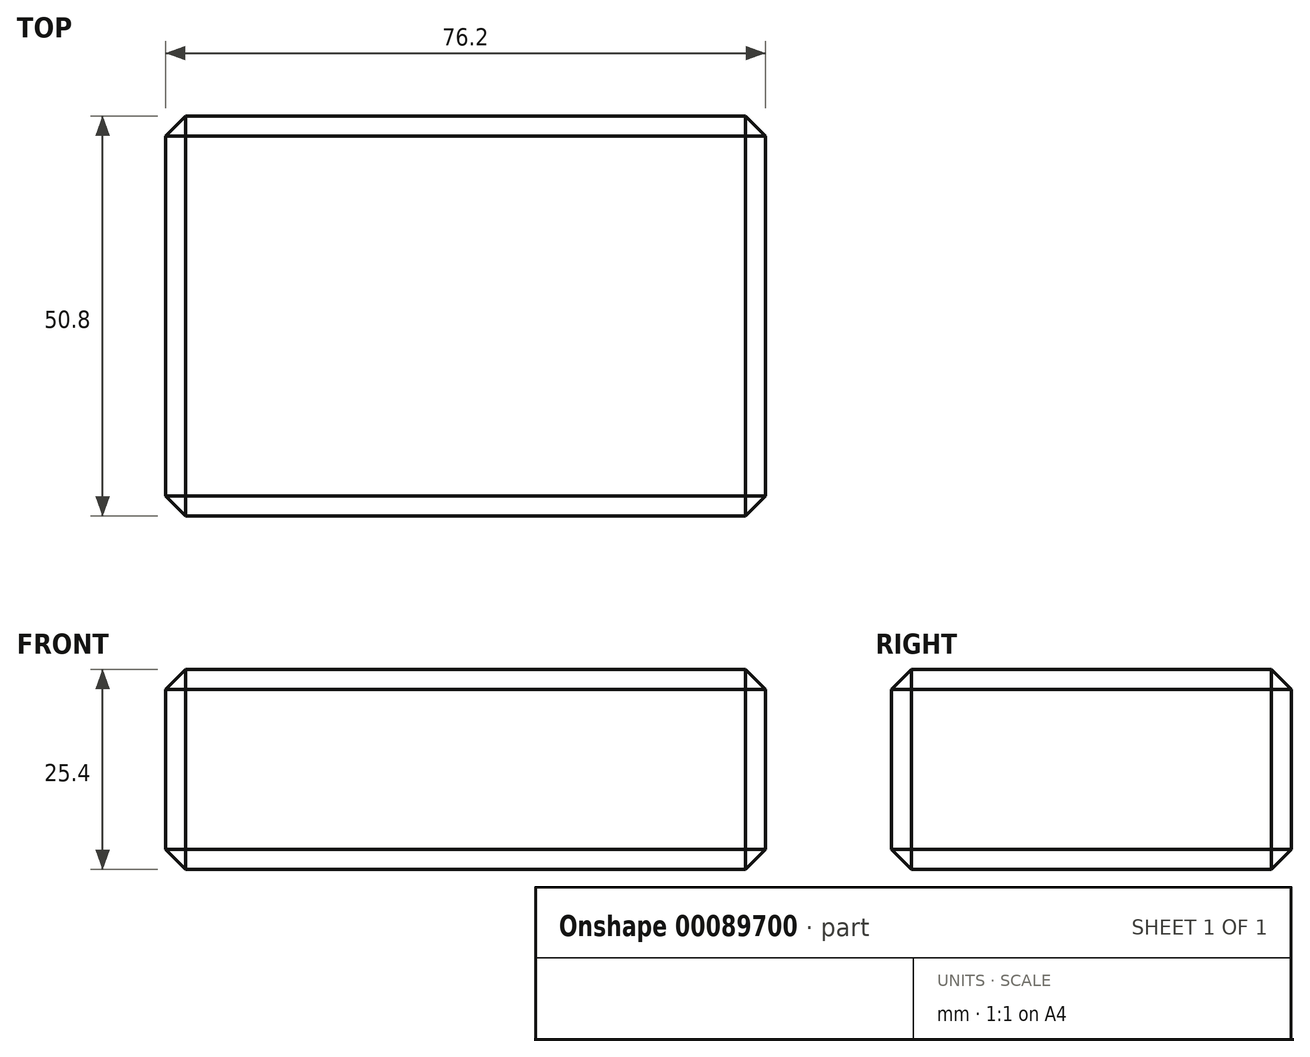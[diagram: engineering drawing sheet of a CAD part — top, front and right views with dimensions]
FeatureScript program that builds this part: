
annotation { "Feature Type Name" : "Feature", "Feature Type Description" : "" }
export const myFeature = defineFeature(function(context is Context, id is Id, definition is map)
    precondition{}
    {
        {
            var Q0;
            Q0=qCreatedBy(makeId("Top.planeOp"),FACE);
            var sketch = newSketch(context, id + "F0", { "sketchPlane" : qUnion([Q0])});
            skLineSegment(sketch, "E0.bottom", {"start": v(0, 0) * mm, "end": v(-76.2, 0) * mm});
            skLineSegment(sketch, "E0.top", {"start": v(0, -50.8) * mm, "end": v(-76.2, -50.8) * mm});
            skLineSegment(sketch, "E0.left", {"start": v(0, 0) * mm, "end": v(0, -50.8) * mm});
            skLineSegment(sketch, "E0.right", {"start": v(-76.2, 0) * mm, "end": v(-76.2, -50.8) * mm});
            skSolve(sketch);
        }
        {
            var Q0;
            Q0=makeQuery(id+"F0.imprint","IMPRINT",FACE,{"disambiguationData":[TD([[makeQuery(id+"F0.imprint","IMPRINT",EDGE,{"derivedFrom":sQuery(id+"F0.wireOp",EDGE,"E0.bottom")}),1.0]])]});
            extrude(context, id + "F1", {"entities" : qUnion([Q0]), "depth" : 25.4 * mm});
        }
        {
            var Q0;
            Q0=makeQuery(id+"F1.opExtrude","CAP_EDGE",EDGE,{"disambiguationData":[OSD([sQuery(id+"F0.wireOp",EDGE,"E0.right")])],"isStart":false});
            var Q1;
            Q1=makeQuery(id+"F1.opExtrude","CAP_EDGE",EDGE,{"disambiguationData":[OSD([sQuery(id+"F0.wireOp",EDGE,"E0.top")])],"isStart":false});
            var Q2;
            Q2=makeQuery(id+"F1.opExtrude","SWEPT_EDGE",EDGE,{"disambiguationData":[OSD([sQuery(id+"F0.wireOp",EDGE,"E0.top"),sQuery(id+"F0.wireOp",EDGE,"E0.right")])]});
            var Q3;
            Q3=makeQuery(id+"F1.opExtrude","CAP_EDGE",EDGE,{"disambiguationData":[OSD([sQuery(id+"F0.wireOp",EDGE,"E0.top")])],"isStart":true});
            var Q4;
            Q4=makeQuery(id+"F1.opExtrude","SWEPT_EDGE",EDGE,{"disambiguationData":[OSD([sQuery(id+"F0.wireOp",EDGE,"E0.top"),sQuery(id+"F0.wireOp",EDGE,"E0.left")])]});
            var Q5;
            Q5=makeQuery(id+"F1.opExtrude","CAP_EDGE",EDGE,{"disambiguationData":[OSD([sQuery(id+"F0.wireOp",EDGE,"E0.left")])],"isStart":false});
            var Q6;
            Q6=makeQuery(id+"F1.opExtrude","CAP_EDGE",EDGE,{"disambiguationData":[OSD([sQuery(id+"F0.wireOp",EDGE,"E0.bottom")])],"isStart":false});
            var Q7;
            Q7=makeQuery(id+"F1.opExtrude","SWEPT_FACE",FACE,{"disambiguationData":[OSD([sQuery(id+"F0.wireOp",EDGE,"E0.right")])]});
            var Q8;
            Q8=makeQuery(id+"F1.opExtrude","CAP_EDGE",EDGE,{"disambiguationData":[OSD([sQuery(id+"F0.wireOp",EDGE,"E0.bottom")])],"isStart":true});
            var Q9;
            Q9=makeQuery(id+"F1.opExtrude","CAP_EDGE",EDGE,{"disambiguationData":[OSD([sQuery(id+"F0.wireOp",EDGE,"E0.left")])],"isStart":true});
            var Q10;
            Q10=makeQuery(id+"F1.opExtrude","SWEPT_EDGE",EDGE,{"disambiguationData":[OSD([sQuery(id+"F0.wireOp",EDGE,"E0.bottom"),sQuery(id+"F0.wireOp",EDGE,"E0.left")])]});
            chamfer(context, id + "F2", {"entities" : qUnion([Q0, Q1, Q2, Q3, Q4, Q5, Q6, Q7, Q8, Q9, Q10]), "width" : 2.54 * mm, "tangentPropagation" : true});
        }
    });
